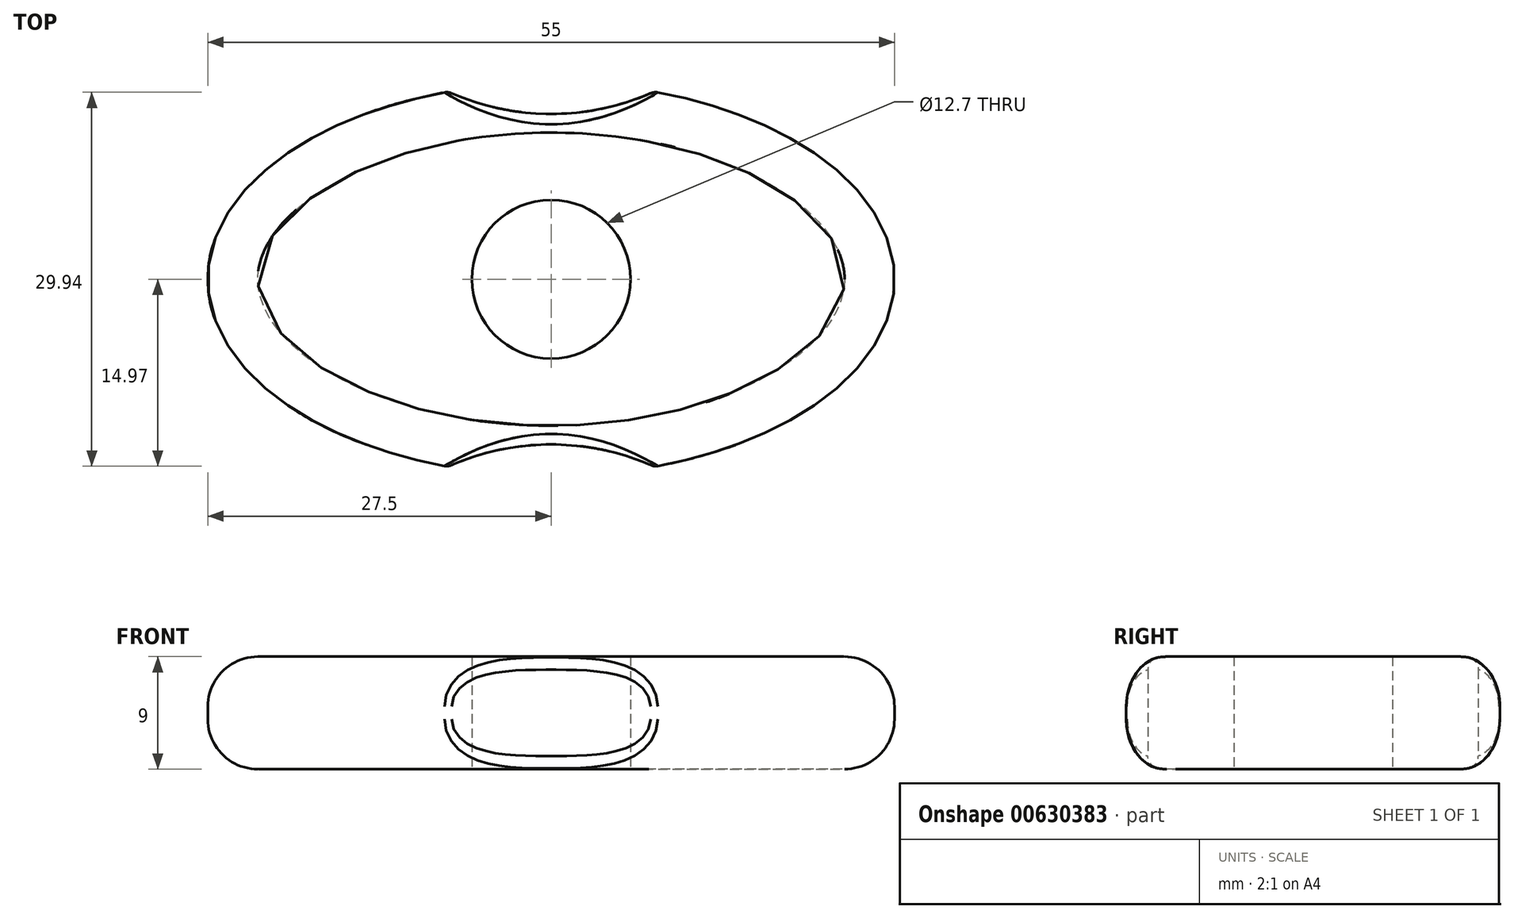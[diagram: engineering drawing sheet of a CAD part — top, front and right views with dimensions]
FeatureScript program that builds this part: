
annotation { "Feature Type Name" : "Feature", "Feature Type Description" : "" }
export const myFeature = defineFeature(function(context is Context, id is Id, definition is map)
    precondition{}
    {
        {
            var Q0;
            Q0=qCreatedBy(makeId("Top.planeOp"),FACE);
            var sketch = newSketch(context, id + "F0", { "sketchPlane" : qUnion([Q0])});
            skEllipticalArc(sketch, "E0", {});
            skCircle(sketch, "E1", {"center": v(0, 0) * mm, "radius": 6.35 * mm});
            skArc(sketch, "E2", {"start": v(8.24, -15) * mm, "mid": v(0, -13.23) * mm, "end": v(-8.24, -15) * mm});
            skArc(sketch, "E3", {"start": v(-8.24, 15) * mm, "mid": v(0, 13.23) * mm, "end": v(8.24, 15) * mm});
            skEllipticalArc(sketch, "E4.trimOffspring", {});
            skPoint(sketch, "E5.center.orphan", {"position": v(0, -15.73) * mm});
            skPoint(sketch, "E6.center.orphan", {"position": v(0, 15.73) * mm});
            const initialGuessF0  = {"E0": [0, 0, 0, -1, 0.015729341262139308, 0.0275, 3.4459625556918185, 5.978815405077561], "E4.trimOffspring": [0, 0, 0, -1, 0.015729341262139308, 0.0275, 0.3043699021020245, 2.8372227514877677]};
            skSetInitialGuess(sketch, initialGuessF0);
            skSolve(sketch);
        }
        {
            var Q0;
            Q0=makeQuery(id+"F0.imprint","IMPRINT",FACE,{"disambiguationData":[TD([[makeQuery(id+"F0.imprint","IMPRINT",EDGE,{"derivedFrom":sQuery(id+"F0.wireOp",EDGE,"E0")}),1.0]])]});
            extrude(context, id + "F1", {"entities" : qUnion([Q0]), "depth" : 9 * mm, "offsetDistance" : 25 * mm});
        }
        {
            var Q0;
            Q0=makeQuery(id+"F1.opExtrude","CAP_EDGE",EDGE,{"disambiguationData":[OSD([sQuery(id+"F0.wireOp",EDGE,"E4.trimOffspring")])],"isStart":true});
            var Q1;
            Q1=makeQuery(id+"F1.opExtrude","CAP_EDGE",EDGE,{"disambiguationData":[OSD([sQuery(id+"F0.wireOp",EDGE,"E0")])],"isStart":true});
            fillet(context, id + "F2", {"entities" : qUnion([Q0, Q1]), "radius" : 4 * mm, "tangentPropagation" : true, "allowEdgeOverflow" : false});
        }
        {
            var Q0;
            Q0=makeQuery(id+"F1.opExtrude","CAP_EDGE",EDGE,{"disambiguationData":[OSD([sQuery(id+"F0.wireOp",EDGE,"E4.trimOffspring")])],"isStart":false});
            var Q1;
            Q1=makeQuery(id+"F1.opExtrude","CAP_EDGE",EDGE,{"disambiguationData":[OSD([sQuery(id+"F0.wireOp",EDGE,"E0")])],"isStart":false});
            fillet(context, id + "F3", {"entities" : qUnion([Q0, Q1]), "radius" : 4 * mm, "tangentPropagation" : true, "allowEdgeOverflow" : false});
        }
        {
            var Q0;
            Q0=makeQuery(id+"F3.opFillet","BLEND_EDGE",EDGE,{"blendedFrom":[makeQuery(id+"F1.opExtrude","CAP_EDGE",EDGE,{"disambiguationData":[OSD([sQuery(id+"F0.wireOp",EDGE,"E4.trimOffspring")])],"isStart":false}),makeQuery(id+"F1.opExtrude","SWEPT_FACE",FACE,{"disambiguationData":[OSD([sQuery(id+"F0.wireOp",EDGE,"E2")])]})],"blendedInto":[makeQuery(id+"F1.opExtrude","SWEPT_FACE",FACE,{"disambiguationData":[OSD([sQuery(id+"F0.wireOp",EDGE,"E2")])]})]});
            var Q1;
            Q1=makeQuery(id+"F2.opFillet","BLEND_EDGE",EDGE,{"blendedFrom":[makeQuery(id+"F1.opExtrude","CAP_EDGE",EDGE,{"disambiguationData":[OSD([sQuery(id+"F0.wireOp",EDGE,"E4.trimOffspring")])],"isStart":true}),makeQuery(id+"F1.opExtrude","SWEPT_FACE",FACE,{"disambiguationData":[OSD([sQuery(id+"F0.wireOp",EDGE,"E2")])]})],"blendedInto":[makeQuery(id+"F1.opExtrude","SWEPT_FACE",FACE,{"disambiguationData":[OSD([sQuery(id+"F0.wireOp",EDGE,"E2")])]})]});
            var Q2;
            Q2=makeQuery(id+"F1.opExtrude","SWEPT_FACE",FACE,{"disambiguationData":[OSD([sQuery(id+"F0.wireOp",EDGE,"E2")])]});
            fillet(context, id + "F4", {"entities" : qUnion([Q0, Q1, Q2]), "radius" : 1 * mm, "tangentPropagation" : true, "allowEdgeOverflow" : false});
        }
        {
            var Q0;
            Q0=makeQuery(id+"F2.opFillet","BLEND_EDGE",EDGE,{"blendedFrom":[makeQuery(id+"F1.opExtrude","CAP_EDGE",EDGE,{"disambiguationData":[OSD([sQuery(id+"F0.wireOp",EDGE,"E4.trimOffspring")])],"isStart":true}),makeQuery(id+"F1.opExtrude","SWEPT_FACE",FACE,{"disambiguationData":[OSD([sQuery(id+"F0.wireOp",EDGE,"E3")])]})],"blendedInto":[makeQuery(id+"F1.opExtrude","SWEPT_FACE",FACE,{"disambiguationData":[OSD([sQuery(id+"F0.wireOp",EDGE,"E3")])]})]});
            var Q1;
            Q1=makeQuery(id+"F3.opFillet","BLEND_EDGE",EDGE,{"blendedFrom":[makeQuery(id+"F1.opExtrude","CAP_EDGE",EDGE,{"disambiguationData":[OSD([sQuery(id+"F0.wireOp",EDGE,"E4.trimOffspring")])],"isStart":false}),makeQuery(id+"F1.opExtrude","SWEPT_FACE",FACE,{"disambiguationData":[OSD([sQuery(id+"F0.wireOp",EDGE,"E3")])]})],"blendedInto":[makeQuery(id+"F1.opExtrude","SWEPT_FACE",FACE,{"disambiguationData":[OSD([sQuery(id+"F0.wireOp",EDGE,"E3")])]})]});
            var Q2;
            Q2=makeQuery(id+"F1.opExtrude","SWEPT_EDGE",EDGE,{"disambiguationData":[OSD([sQuery(id+"F0.wireOp",EDGE,"E3"),sQuery(id+"F0.wireOp",EDGE,"E4.trimOffspring")])]});
            var Q3;
            Q3=makeQuery(id+"F1.opExtrude","SWEPT_EDGE",EDGE,{"disambiguationData":[OSD([sQuery(id+"F0.wireOp",EDGE,"E0"),sQuery(id+"F0.wireOp",EDGE,"E3")])]});
            fillet(context, id + "F5", {"entities" : qUnion([Q0, Q1, Q2, Q3]), "radius" : 1 * mm, "tangentPropagation" : true, "allowEdgeOverflow" : false});
        }
    });
